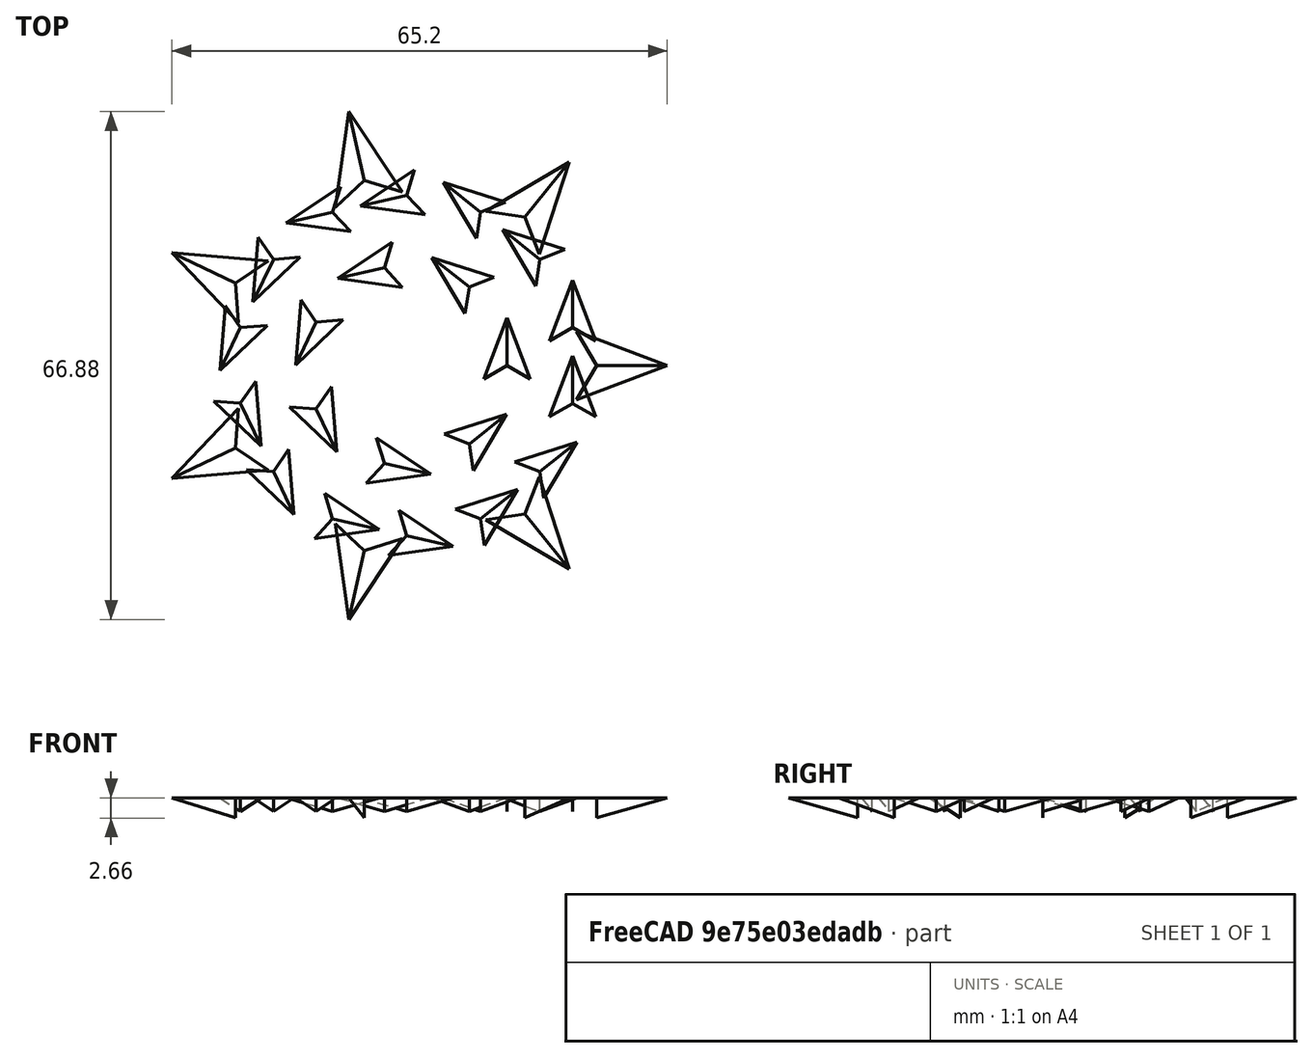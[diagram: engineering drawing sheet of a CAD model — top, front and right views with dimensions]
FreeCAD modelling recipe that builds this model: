
FCSTD DOCUMENT  (FreeCAD 0.21R32457 (Git))
Label: 10mm lens packing
License: All rights reserved
LicenseURL: http://en.wikipedia.org/wiki/All_rights_reserved
objects: Part::FeaturePython×15, Sketcher::SketchObject×7, Part::Compound×2, App::DocumentObjectGroup×1
note: 24 computed .brp shape members not serialized (recipe doc carries the construction recipe); baked Part::Feature solids carry a one-line shape summary decoded from their .brp

FEATURE [Sketcher::SketchObject] Sketch  label="cam lens (Sketch)"
  FullyConstrained = true
  sketch-geometry (1):
    g0: Circle CenterX=0 CenterY=0 CenterZ=0 NormalX=0 NormalY=0 NormalZ=1 AngleXU=0 Radius=7.25
  constraints (2):
    c: Coincident(g0,g-1)
    c: Diameter(g0) = 14.5
FEATURE [Part::FeaturePython] PolarArray  # WARN: FeaturePython — macro-defined, semantics opaque (R4)
  Alignment = 0
  AttacherType = Attacher::AttachEngine3D
  CellStart = A1
  Count = 7
  DistributionLaw = 0
  EndInclusive = false
  ExposePlacement = false
  FlipX = false
  FlipZ = false
  GeneratorMode = 0
  MarkerShape = 1
  MarkerSize = 0
  NumElements = 7
  OrientMode = 2
  Radius = 25
  Reverse = false
  SpanEnd = 360
  SpanStart = 0
  Step = 51.4286
  Type = lattice2PolarArray2.PolarArray
  UseArcRadius = false
  UseArcRange = 0
  VSGVersion = 1
  Values = 0.0 | 51.42857142857143 | 102.85714285714286 | 154.28571428571428 | 205.71428571428572 | 257.14285714285717 | 308.57142857142856
  ValuesSource = 2
  isLattice = 1
FEATURE [Sketcher::SketchObject] Sketch001
  ExternalGeometry = -> [Sketch,PolarArray]
  FullyConstrained = false
  sketch-geometry (4):
    g0: Circle CenterX=13.2133 CenterY=0 CenterZ=0 NormalX=0 NormalY=0 NormalZ=1 AngleXU=0 Radius=5
    g1: Circle CenterX=21.8736 CenterY=5 CenterZ=0 NormalX=0 NormalY=0 NormalZ=1 AngleXU=0 Radius=5
    g2: Circle CenterX=21.8736 CenterY=-5 CenterZ=0 NormalX=0 NormalY=0 NormalZ=1 AngleXU=0 Radius=5
    g3: LineSegment StartX=39.5093 StartY=19.0267 StartZ=0 EndX=0 EndY=0 EndZ=0
  constraints (9):
    c: Equal(g1,g0)
    c: Diameter(g1) = 10
    c: Symmetric(g2,g1,g-1)
    c: PointOnObject(g0,g-1)
    c: Tangent(g0,g1)
    c: Symmetric(g-5,g-4,g3)
    c: PointOnObject(g3,g-2)
    c: Tangent(g2,g1)
    c: Equal(g2,g1)
FEATURE [Part::FeaturePython] Populate  label="Populate PolarArray with Sketch001"  # WARN: FeaturePython — macro-defined, semantics opaque (R4)
  Copying = 0
  ExposePlacement = false
  MarkerShape = 1
  MarkerSize = 0
  NumElements = 0
  Object = -> Sketch001
  OutputCompounding = 1
  PlacementsTo = -> PolarArray
  Referencing = 1
  Type = lattice2PopulateCopies.LatticePopulateCopies
  isLattice = 0
FEATURE [Part::FeaturePython] Downgrade  label="Leaves of Populate PolarArray with Sketch001"  # WARN: FeaturePython — macro-defined, semantics opaque (R4)
  Base = -> Populate
  Mode = 1
FEATURE [Sketcher::SketchObject] Sketch002  label="ext bounding (Sketch002)"
  ExternalGeometry = -> [Downgrade]
  FullyConstrained = true
  sketch-geometry (1):
    g0: Circle CenterX=-5.833e-13 CenterY=-1.0962e-12 CenterZ=0 NormalX=0 NormalY=0 NormalZ=1 AngleXU=0 Radius=27.4378
  constraints (4):
    c: Tangent(g0,g-5)
    c: Tangent(g-3,g0)
    c: Tangent(g-4,g0)
    c: Diameter(g0) = 54.8756
FEATURE [Part::FeaturePython] Placment  # WARN: FeaturePython — macro-defined, semantics opaque (R4)
  AttacherType = Attacher::AttachEngine3D
  ExposePlacement = true
  MapMode = 11
  MarkerShape = 1
  MarkerSize = 10
  NumElements = 1
  Placement = pos=(13.2133,0,0) rot=(0,0,1;1.5708rad)
  Support = -> [Downgrade]
  Type = lattice2AttachablePlacement.AttachablePlacement
  isLattice = 1
FEATURE [Part::FeaturePython] PlacementSubsequence  label="LED placements (PlacementSubsequence)"  # WARN: FeaturePython — macro-defined, semantics opaque (R4)
  Base = -> Placment
  CycleMode = 0
  ExposePlacement = false
  MarkerShape = 1
  MarkerSize = 0
  NumElements = 21
  Type = lattice2AttachablePlacement.AttachedPlacementSubsequence
  isLattice = 1
FEATURE [Sketcher::SketchObject] Sketch003  label="led footprint extents (Sketch003)"
  ExternalGeometry = -> [Downgrade]
  FullyConstrained = true
  sketch-geometry (1):
    g0: Circle CenterX=13.2133 CenterY=0 CenterZ=0 NormalX=0 NormalY=0 NormalZ=1 AngleXU=0 Radius=2.64
  constraints (2):
    c: Coincident(g0,g-3)
    c: Diameter(g0) = 5.28
FEATURE [Part::FeaturePython] Populate001  label="Populate PlacementSubsequence with Sketch003"  # WARN: FeaturePython — macro-defined, semantics opaque (R4)
  Copying = 0
  ExposePlacement = false
  MarkerShape = 1
  MarkerSize = 0
  NumElements = 0
  Object = -> Sketch003
  OutputCompounding = 1
  PlacementsTo = -> PlacementSubsequence
  Referencing = 1
  Type = lattice2PopulateCopies.LatticePopulateCopies
  isLattice = 0
FEATURE [Sketcher::SketchObject] Sketch004  label="fill zones (Sketch004)"
  ExternalGeometry = -> [Sketch002,Sketch]
  FullyConstrained = true
  sketch-geometry (11):
    g0: Circle CenterX=0 CenterY=0 CenterZ=0 NormalX=0 NormalY=0 NormalZ=1 AngleXU=0 Radius=27.0378
    g1: Circle CenterX=0 CenterY=0 CenterZ=0 NormalX=0 NormalY=0 NormalZ=1 AngleXU=0 Radius=17.1939
    g2: Circle CenterX=0 CenterY=0 CenterZ=0 NormalX=0 NormalY=0 NormalZ=1 AngleXU=0 Radius=17.4939
    g3: Circle CenterX=0 CenterY=0 CenterZ=0 NormalX=0 NormalY=0 NormalZ=1 AngleXU=0 Radius=7.65
    g4: GeomPoint X=7.65 Y=0 Z=0
    g5: GeomPoint X=17.1939 Y=0 Z=0
    g6: GeomPoint X=7.25 Y=0 Z=0
    g7: GeomPoint X=17.4939 Y=0 Z=0
    g8: GeomPoint X=27.0378 Y=0 Z=0
    g9: GeomPoint X=27.4378 Y=0 Z=0
    g10: GeomPoint X=17.3439 Y=0 Z=0
  constraints (20):
    c: Coincident(g0,g1)
    c: Coincident(g0,g2)
    c: Coincident(g0,g3)
    c: Coincident(g0,g-4)
    c: PointOnObject(g6,g-4)
    c: PointOnObject(g6,g-1)
    c: PointOnObject(g4,g3)
    c: PointOnObject(g4,g-1)
    c: PointOnObject(g5,g1)
    c: PointOnObject(g5,g-1)
    c: PointOnObject(g8,g0)
    c: PointOnObject(g8,g-1)
    c: PointOnObject(g9,g-3)
    c: PointOnObject(g9,g-1)
    c: Symmetric(g9,g6,g10)
    c: PointOnObject(g7,g2)
    c: Symmetric(g5,g7,g10)
    c: DistanceX(g6,g4) = 0.4
    c: DistanceX(g8,g9) = 0.4
    c: DistanceX(g5,g7) = 0.3
FEATURE [Part::Compound] Compound
  Links = -> [Sketch002,Sketch,Populate001,Downgrade,Sketch004]
FEATURE [Sketcher::SketchObject] Sketch005  label="connector flap (Sketch005)"
  ExternalGeometry = -> [Sketch002]
  FullyConstrained = false
  sketch-geometry (10):
    g0: LineSegment StartX=-29.2644 StartY=29.2644 StartZ=0 EndX=0 EndY=0 EndZ=0
    g1: LineSegment StartX=-24.612 StartY=26.3531 StartZ=0 EndX=-26.3531 EndY=24.612 EndZ=0
    g2: ArcOfCircle CenterX=-24.3953 CenterY=22.6541 CenterZ=0 NormalX=0 NormalY=0 NormalZ=1 AngleXU=0 Radius=2.76881 StartAngle=2.35619 EndAngle=3.92699
    g3: LineSegment StartX=-26.3531 StartY=20.6963 StartZ=0 EndX=-25.9973 EndY=20.3405 EndZ=0
    g4: ArcOfCircle CenterX=-31.0773 CenterY=15.2605 CenterZ=0 NormalX=0 NormalY=0 NormalZ=1 AngleXU=0 Radius=7.18422 StartAngle=5.82672 EndAngle=7.06858
    g5: LineSegment StartX=-20.6963 StartY=26.3531 StartZ=0 EndX=-20.3405 EndY=25.9973 EndZ=0
    g6: ArcOfCircle CenterX=-15.2605 CenterY=31.0773 CenterZ=0 NormalX=0 NormalY=0 NormalZ=1 AngleXU=0 Radius=7.18422 StartAngle=3.92699 EndAngle=5.16885
    g7: ArcOfCircle CenterX=-22.6541 CenterY=24.3953 CenterZ=0 NormalX=0 NormalY=0 NormalZ=1 AngleXU=0 Radius=2.76881 StartAngle=0.785398 EndAngle=2.35619
    g8: GeomPoint X=-19.4014 Y=19.4014 Z=0
    g9: GeomPoint X=-25.4826 Y=25.4826 Z=0
  constraints (20):
    c: Coincident(g0,g-1)
    c: Angle(g0) = -0.785398
    c: Tangent(g1,g2) = -1.5708
    c: Tangent(g2,g3) = -1.5708
    c: Tangent(g3,g4) = 1.5708
    c: Tangent(g5,g6) = -1.5708
    c: Symmetric(g6,g4,g0)
    c: Tangent(g6,g-3) = 1.5708
    c: Tangent(g4,g-3) = 1.5708
    c: Tangent(g7,g5) = 1.5708
    c: Tangent(g7,g1) = -1.5708
    c: Symmetric(g7,g2,g0)
    c: Parallel(g5,g0)
    c: Equal(g2,g7)
    c: PointOnObject(g8,g0)
    c: PointOnObject(g8,g-3)
    c: PointOnObject(g9,g0)
    c: PointOnObject(g9,g1)
    c: Distance(g9,g8) = 8.6
    c: Distance(g2,g5) = 8
FEATURE [Part::FeaturePython] Array  # Draft array (typed FeaturePython)
  Angle = 360
  ArrayType = 1
  Axis = (0,0,1)
  Base = -> Sketch005
  Center = (0,0,0)
  Count = 4
  Fuse = false
  IntervalAxis = (0,0,0)
  IntervalX = (50,0,0)
  IntervalY = (0,50,0)
  IntervalZ = (0,0,50)
  NumberCircles = 3
  NumberPolar = 4
  NumberX = 2
  NumberY = 2
  NumberZ = 1
  RadialDistance = 50
  Symmetry = 1
  TangentialDistance = 25
FEATURE [Part::FeaturePython] Array_child0  label="Array.0"  # WARN: FeaturePython — macro-defined, semantics opaque (R4)
  Base = -> Array
  FilterType = 1
  Invert = false
  OverrideMaxVal = 0
  WindowFrom = 80
  WindowTo = 100
  items = 0
FEATURE [Part::FeaturePython] Array_child1  label="Array.1"  # WARN: FeaturePython — macro-defined, semantics opaque (R4)
  Base = -> Array
  FilterType = 1
  Invert = false
  OverrideMaxVal = 0
  WindowFrom = 80
  WindowTo = 100
  items = 1
FEATURE [Part::FeaturePython] Array_child2  label="Array.2"  # WARN: FeaturePython — macro-defined, semantics opaque (R4)
  Base = -> Array
  FilterType = 1
  Invert = false
  OverrideMaxVal = 0
  WindowFrom = 80
  WindowTo = 100
  items = 2
FEATURE [Part::FeaturePython] Array_child3  label="Array.3"  # WARN: FeaturePython — macro-defined, semantics opaque (R4)
  Base = -> Array
  FilterType = 1
  Invert = false
  OverrideMaxVal = 0
  WindowFrom = 80
  WindowTo = 100
  items = 3
FEATURE [App::DocumentObjectGroup] GrExplode_Array  label="Exploded Array"
  Group = -> [Array_child0,Array_child1,Array_child2,Array_child3]
FEATURE [Part::FeaturePython] Connect  # WARN: FeaturePython — macro-defined, semantics opaque (R4)
  Objects = -> [Array_child0,Sketch002]
  Tolerance = 0
FEATURE [Part::FeaturePython] Connect001  # WARN: FeaturePython — macro-defined, semantics opaque (R4)
  Objects = -> [Connect,Array_child1]
  Tolerance = 0
FEATURE [Part::FeaturePython] Connect002  # WARN: FeaturePython — macro-defined, semantics opaque (R4)
  Objects = -> [Connect001,Array_child3]
  Tolerance = 0
FEATURE [Part::FeaturePython] Connect003  # WARN: FeaturePython — macro-defined, semantics opaque (R4)
  Objects = -> [Connect002,Array_child2]
  Tolerance = 0
FEATURE [Part::Compound] Compound001  label="board outline"
  Links = -> [Sketch,Connect003]
FEATURE [Sketcher::SketchObject] Sketch006
  FullyConstrained = false
  sketch-geometry (2):
    g0: LineSegment StartX=-35.5698 StartY=35.5698 StartZ=0 EndX=0 EndY=0 EndZ=0
    g1: Circle CenterX=-22 CenterY=22 CenterZ=0 NormalX=0 NormalY=0 NormalZ=1 AngleXU=0 Radius=1.6
  constraints (5):
    c: Angle(g0) = -0.785398
    c: Coincident(g0,g-1)
    c: Diameter(g1) = 3.2
    c: PointOnObject(g1,g0)
    c: DistanceX(g-2,g1) = -22
